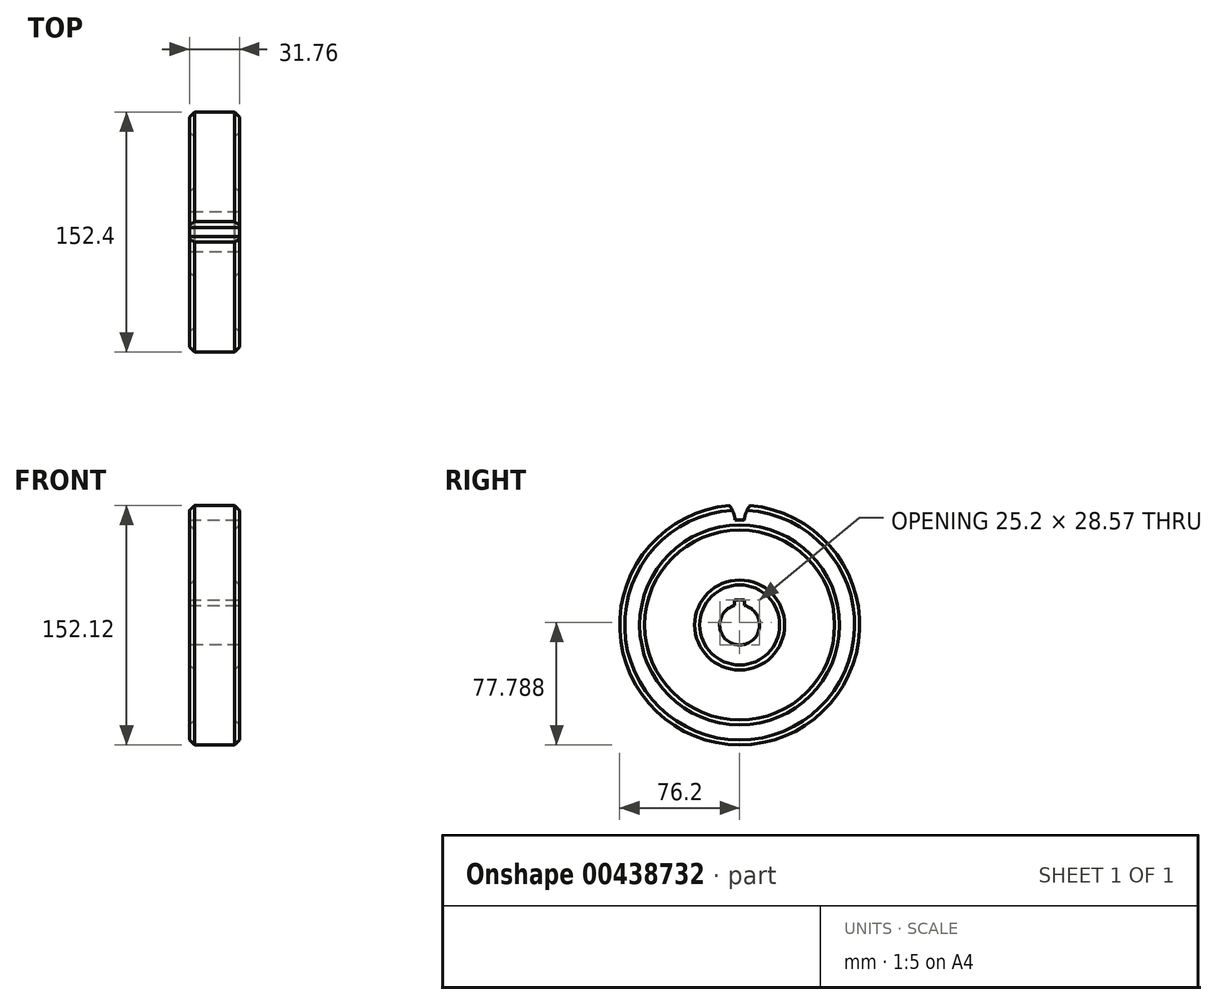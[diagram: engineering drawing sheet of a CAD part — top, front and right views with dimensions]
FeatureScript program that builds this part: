
annotation { "Feature Type Name" : "Feature", "Feature Type Description" : "" }
export const myFeature = defineFeature(function(context is Context, id is Id, definition is map)
    precondition{}
    {
        {
            var Q0;
            Q0=qCreatedBy(makeId("Front.planeOp"),FACE);
            var sketch = newSketch(context, id + "F0", { "sketchPlane" : qUnion([Q0])});
            skLineSegment(sketch, "E0", {"start": v(0, 43.43) * mm, "end": v(0, -20.07) * mm});
            skLineSegment(sketch, "E1", {"start": v(0, 43.43) * mm, "end": v(12.7, 43.43) * mm});
            skLineSegment(sketch, "E2", {"start": v(12.7, 43.43) * mm, "end": v(15.87, 40.26) * mm});
            skLineSegment(sketch, "E3", {"start": v(15.87, 40.26) * mm, "end": v(15.87, 30.73) * mm});
            skLineSegment(sketch, "E4", {"start": v(15.88, 30.73) * mm, "end": v(12.7, 27.56) * mm});
            skLineSegment(sketch, "E5", {"start": v(12.7, 27.56) * mm, "end": v(12.7, -4.2) * mm});
            skLineSegment(sketch, "E6", {"start": v(12.7, -4.2) * mm, "end": v(15.88, -7.37) * mm});
            skLineSegment(sketch, "E7", {"start": v(15.87, -7.37) * mm, "end": v(15.87, -20.07) * mm});
            skLineSegment(sketch, "E8", {"start": v(15.87, -20.07) * mm, "end": v(0, -20.07) * mm});
            skLineSegment(sketch, "E9", {"start": v(0, -20.07) * mm, "end": v(0, -32.77) * mm});
            skLineSegment(sketch, "E10", {"start": v(0, -32.77) * mm, "end": v(17.25, -32.77) * mm});
            skLineSegment(sketch, "E11.MirrorCS", {"start": v(0, 43.43) * mm, "end": v(-12.7, 43.43) * mm});
            skLineSegment(sketch, "E12.MirrorCS", {"start": v(-12.7, 43.43) * mm, "end": v(-15.87, 40.26) * mm});
            skLineSegment(sketch, "E13.MirrorCS", {"start": v(-15.88, 40.26) * mm, "end": v(-15.88, 30.73) * mm});
            skLineSegment(sketch, "E14.MirrorCS", {"start": v(-15.88, 30.73) * mm, "end": v(-12.7, 27.56) * mm});
            skLineSegment(sketch, "E15.MirrorCS", {"start": v(-12.7, 27.56) * mm, "end": v(-12.7, -4.2) * mm});
            skLineSegment(sketch, "E16.MirrorCS", {"start": v(-12.7, -4.2) * mm, "end": v(-15.87, -7.37) * mm});
            skLineSegment(sketch, "E17.MirrorCS", {"start": v(-15.88, -7.37) * mm, "end": v(-15.88, -20.07) * mm});
            skLineSegment(sketch, "E18.MirrorCS", {"start": v(-15.88, -20.07) * mm, "end": v(0, -20.07) * mm});
            skSolve(sketch);
        }
        {
            var Q0;
            Q0=makeQuery(id+"F0.imprint","IMPRINT",FACE,{"disambiguationData":[TD([[makeQuery(id+"F0.imprint","IMPRINT",EDGE,{"derivedFrom":sQuery(id+"F0.wireOp",EDGE,"E0")}),1.0]])]});
            var Q1;
            Q1=makeQuery(id+"F0.imprint","IMPRINT",FACE,{"disambiguationData":[TD([[makeQuery(id+"F0.imprint","IMPRINT",EDGE,{"derivedFrom":sQuery(id+"F0.wireOp",EDGE,"E0")}),-1.0]])]});
            var Q2;
            Q2=sQuery(id+"F0.wireOp",EDGE,"E10");
            revolve(context, id + "F1", {"entities" : qUnion([Q0, Q1]), "axis" : qUnion([Q2]), "revolveType" : RevolveType.FULL});
        }
        {
            var Q0;
            Q0=makeQuery(id+"F1.opRevolve","SWEPT_FACE",FACE,{"disambiguationData":[OSD([sQuery(id+"F0.wireOp",EDGE,"E3")])]});
            var sketch = newSketch(context, id + "F2", { "sketchPlane" : qUnion([Q0])});
            skLineSegment(sketch, "E19", {"start": v(0, -32.77) * mm, "end": v(0, 152.37) * mm});
            skLineSegment(sketch, "E20", {"start": v(0, 33.9) * mm, "end": v(2.86, 33.9) * mm});
            skArc(sketch, "E21", {"start": v(6.54, 43.15) * mm, "mid": v(4.08, 38.77) * mm, "end": v(2.86, 33.9) * mm});
            skLineSegment(sketch, "E22.MirrorCS", {"start": v(0, 33.9) * mm, "end": v(-2.86, 33.9) * mm});
            skArc(sketch, "E23.MirrorCS", {"start": v(-6.54, 43.15) * mm, "mid": v(-4.08, 38.77) * mm, "end": v(-2.86, 33.9) * mm});
            skArc(sketch, "E24.0", {"start": v(6.54, 43.15) * mm, "mid": v(0, 43.43) * mm, "end": v(-6.54, 43.15) * mm});
            skSolve(sketch);
        }
        {
            var Q0;
            {var subQ0=sQuery(id+"F2.wireOp",EDGE,"E24.0");var subQ5=sQuery(id+"F2.wireOp",EDGE,"E23.MirrorCS");var subQ6=makeQuery(id+"F2.imprint","INTERSECT",VERTEX,{"derivedFrom":[subQ5,subQ0]});Q0=makeQuery(id+"F2.imprint","IMPRINT",FACE,{"disambiguationData":[TD([[makeQuery(id+"F2.imprint","IMPRINT",EDGE,{"disambiguationData":[TD([[subQ6,1.0]])],"derivedFrom":subQ0}),1.0]])]});}
            var Q1;
            {var subQ0=sQuery(id+"F2.wireOp",EDGE,"E24.0");var subQ5=sQuery(id+"F2.wireOp",EDGE,"E21");var subQ6=makeQuery(id+"F2.imprint","INTERSECT",VERTEX,{"derivedFrom":[subQ5,subQ0]});Q1=makeQuery(id+"F2.imprint","IMPRINT",FACE,{"disambiguationData":[TD([[makeQuery(id+"F2.imprint","IMPRINT",EDGE,{"disambiguationData":[TD([[subQ6,-1.0]])],"derivedFrom":subQ0}),1.0]])]});}
            var Q2;
            {var subQ0=sQuery(id+"F2.wireOp",EDGE,"E20");Q2=makeQuery(id+"F2.imprint","IMPRINT",FACE,{"disambiguationData":[TD([[makeQuery(id+"F2.imprint","IMPRINT",EDGE,{"derivedFrom":subQ0}),1.0]])]});}
            var Q3;
            {var subQ0=sQuery(id+"F2.wireOp",EDGE,"E22.MirrorCS");Q3=makeQuery(id+"F2.imprint","IMPRINT",FACE,{"disambiguationData":[TD([[makeQuery(id+"F2.imprint","IMPRINT",EDGE,{"derivedFrom":subQ0}),-1.0]])]});}
            extrude(context, id + "F3", {"entities" : qUnion([Q0, Q1, Q2, Q3]), "operationType" : NewBodyOperationType.REMOVE, "endBound" : BoundingType.THROUGH_ALL, "oppositeDirection" : true, "depth" : 50.8 * mm});
        }
        {
            var Q0;
            Q0=makeQuery(id+"F1.opRevolve","SWEPT_FACE",FACE,{"disambiguationData":[OSD([sQuery(id+"F0.wireOp",EDGE,"E7")])]});
            var sketch = newSketch(context, id + "F4", { "sketchPlane" : qUnion([Q0])});
            skLineSegment(sketch, "E25", {"start": v(0, -32.77) * mm, "end": v(0, 38.02) * mm});
            skLineSegment(sketch, "E26", {"start": v(0, -16.9) * mm, "end": v(3.17, -16.9) * mm});
            skLineSegment(sketch, "E27", {"start": v(3.18, -16.9) * mm, "end": v(3.18, -20.47) * mm});
            skLineSegment(sketch, "E28.MirrorCS", {"start": v(0, -16.9) * mm, "end": v(-3.17, -16.9) * mm});
            skLineSegment(sketch, "E29.MirrorCS", {"start": v(-3.17, -16.9) * mm, "end": v(-3.17, -20.47) * mm});
            skArc(sketch, "E30.0", {"start": v(3.18, -20.47) * mm, "mid": v(0, -20.07) * mm, "end": v(-3.17, -20.47) * mm});
            skSolve(sketch);
        }
        {
            var Q0;
            {var subQ0=sQuery(id+"F4.wireOp",EDGE,"E28.MirrorCS");Q0=makeQuery(id+"F4.imprint","IMPRINT",FACE,{"disambiguationData":[TD([[makeQuery(id+"F4.imprint","IMPRINT",EDGE,{"derivedFrom":subQ0}),1.0]])]});}
            var Q1;
            {var subQ0=sQuery(id+"F4.wireOp",EDGE,"E26");Q1=makeQuery(id+"F4.imprint","IMPRINT",FACE,{"disambiguationData":[TD([[makeQuery(id+"F4.imprint","IMPRINT",EDGE,{"derivedFrom":subQ0}),-1.0]])]});}
            extrude(context, id + "F5", {"entities" : qUnion([Q0, Q1]), "operationType" : NewBodyOperationType.REMOVE, "endBound" : BoundingType.THROUGH_ALL, "oppositeDirection" : true, "depth" : 25.4 * mm});
        }
    });
